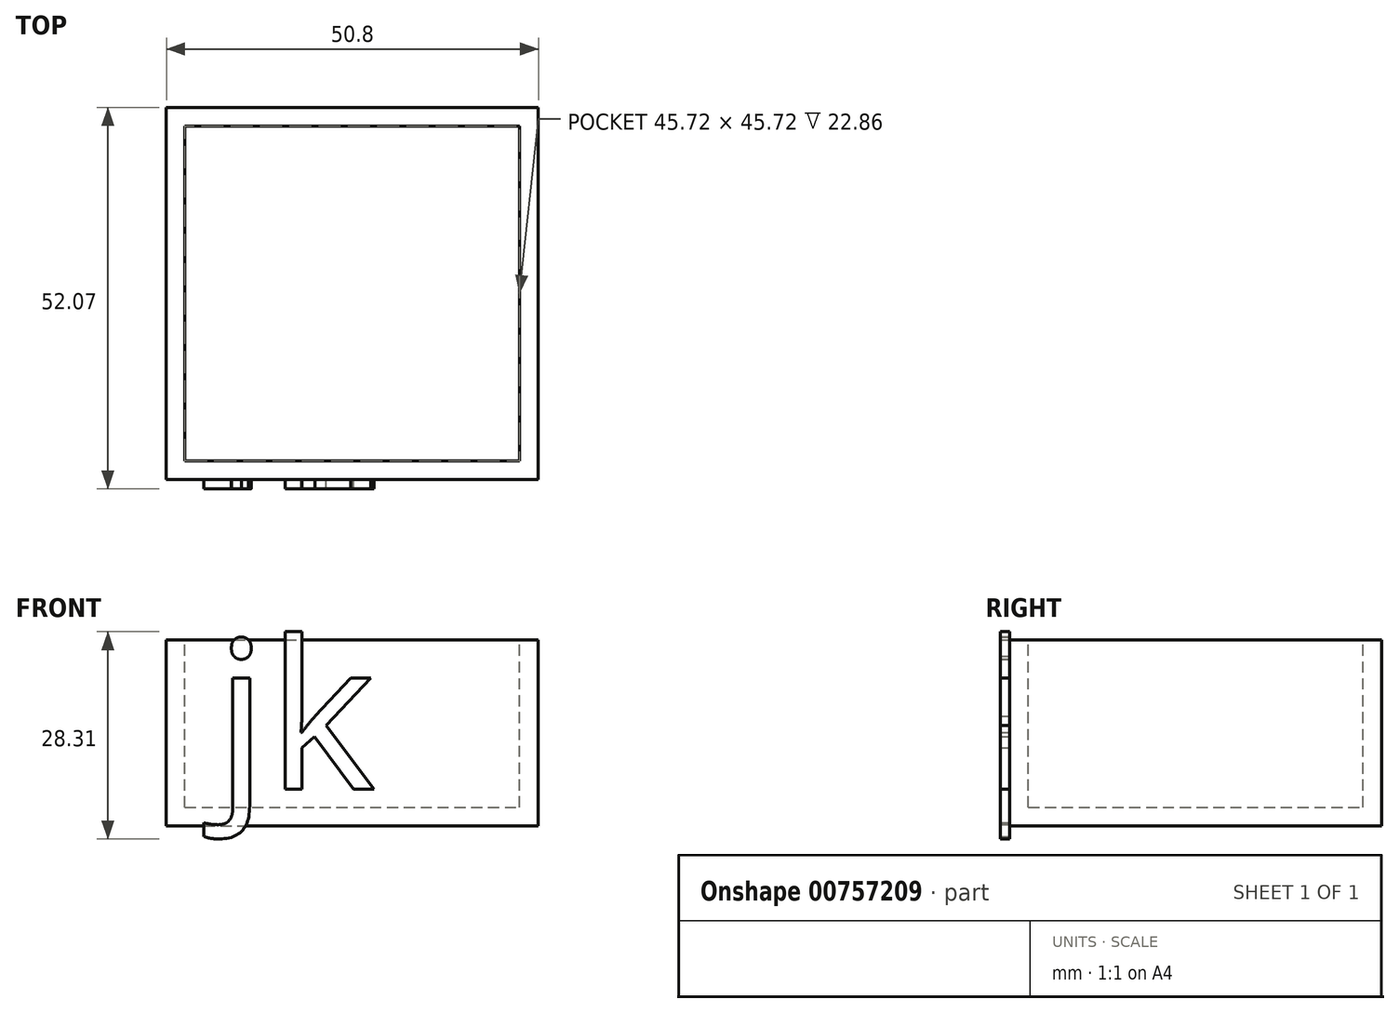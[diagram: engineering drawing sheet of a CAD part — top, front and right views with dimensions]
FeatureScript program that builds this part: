
annotation { "Feature Type Name" : "Feature", "Feature Type Description" : "" }
export const myFeature = defineFeature(function(context is Context, id is Id, definition is map)
    precondition{}
    {
        {
            var Q0;
            Q0=qCreatedBy(makeId("Front.planeOp"),FACE);
            var sketch = newSketch(context, id + "F0", { "sketchPlane" : qUnion([Q0])});
            skLineSegment(sketch, "E0.bottom", {"start": v(-40.94, 3.36) * mm, "end": v(9.86, 3.36) * mm});
            skLineSegment(sketch, "E0.top", {"start": v(-40.94, 28.76) * mm, "end": v(9.86, 28.76) * mm});
            skLineSegment(sketch, "E0.left", {"start": v(-40.94, 3.36) * mm, "end": v(-40.94, 28.76) * mm});
            skLineSegment(sketch, "E0.right", {"start": v(9.86, 3.36) * mm, "end": v(9.86, 28.76) * mm});
            skSolve(sketch);
        }
        {
            var Q0;
            Q0 = qSketchRegion(id + "F0", true);
            extrude(context, id + "F1", {"entities" : qUnion([Q0]), "depth" : 50.8 * mm, "offsetDistance" : 25.4 * mm});
        }
        {
            var Q0;
            Q0=makeQuery(id+"F1.opExtrude","SWEPT_FACE",FACE,{"disambiguationData":[OSD([sQuery(id+"F0.wireOp",EDGE,"E0.top")])]});
            shell(context, id + "F2", {"entities" : qUnion([Q0]), "thickness" : 2.54 * mm});
        }
        {
            var Q0;
            Q0=makeQuery(id+"F1.opExtrude","CAP_FACE",FACE,{"disambiguationData":[OSD([sQuery(id+"F0.wireOp",EDGE,"E0.bottom"),sQuery(id+"F0.wireOp",EDGE,"E0.top"),sQuery(id+"F0.wireOp",EDGE,"E0.left"),sQuery(id+"F0.wireOp",EDGE,"E0.right")])],"isStart":false});
            var sketch = newSketch(context, id + "F3", { "sketchPlane" : qUnion([Q0])});
            skText(sketch, "E1", { "text": "jk", "fontName": "OpenSans-Regular.ttf"});
            const initialGuessF3  = {"E1": [-0.0343, 0.00838, 1, 0, 0.02038]};
            skSetInitialGuess(sketch, initialGuessF3);
            skSolve(sketch);
        }
        {
            var Q0;
            Q0 = qSketchRegion(id + "F3", true);
            extrude(context, id + "F4", {"entities" : qUnion([Q0]), "operationType" : NewBodyOperationType.ADD, "depth" : 1.27 * mm, "offsetDistance" : 25.4 * mm});
        }
    });
